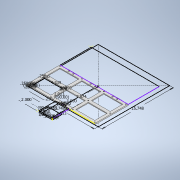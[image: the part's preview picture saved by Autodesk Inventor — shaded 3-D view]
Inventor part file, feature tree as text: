
AUTODESK INVENTOR PART (.ipt)
format: ipt  version: 2020 (Build 240168000, 168)  size: 369,664 bytes
history: native  units: in
note: dims shown in document units (in); Inventor stores cm internally (conversion verified against a paired STEP export)
features: extrude x8, sketch x7, hole x4, pattern_linear x1
ambient origin geometry x8: Origin, YZ Plane, XZ Plane, XY Plane, X Axis, Y Axis, Z Axis, Center Point
bodies: Solid1 (feature_tree)
feature tree (20):
  sketch  "Sketch1"  dims[d0=3.0in d1=2.0in]
  extrude  "Extrusion1"  Depth=2.0in
  hole  "Hole1"  [1 undecoded]
  sketch  "Sketch2"  dims[d2=0.25in d3=1.0in]
  extrude  "Extrusion2"  TaperAngle=0.0deg  [1 undecoded]
  hole  "Hole2"  [1 undecoded]
  extrude  "Extrusion3"  Depth=0.25in
  pattern_linear  "Rectangular Pattern1"  Spacing1=2.9528in  [1 undecoded]
  extrude  "Extrusion4"  Depth=0.25in
  sketch  "Sketch4"  dims[d6=0.5in d7=0.5in]
  extrude  "Extrusion5"  Depth=0.25in
  hole  "Hole3"  [1 undecoded]
  extrude  "Extrusion6"  Depth=0.25in
  extrude  "Extrusion7"  Depth=0.25in
  extrude  "Extrusion8"  Depth=0.25in TaperAngle=0.0deg
  hole  "Hole4"  [1 undecoded]
  sketch  "Sketch3"  dims[d4=1.0in d5=0.0in]
  sketch  "Sketch5"  dims[d8=0.25in d9=0.25in]
  sketch  "Sketch6"  dims[d10=2.9528in]
  sketch  "Sketch7"  dims[d11=90.0deg d12=2.9528in d13=1.0in d14=7.874in d15=90.0deg d16=15.748in d17=15.748in d18=0.25in d19=0.0in d20=0.26in d21=0.5in d22=0.375in d23=0.25in d24=0.5635in d25=1.0in d26=0.8108in d27=0.25in d28=90.0deg d29=0.25in d30=0.25in d31=0.25in d32=4.3386in d33=2.9134in d34=0.25in d35=0.25in d36=0.25in d37=0.25in d38=0.25in d39=0.315in d40=90.0deg d41=0.0787in d42=0.0787in d43=0.0787in d44=0.0787in d45=0.0in d46=0.0in d47=0.203in d48=0.625in d49=0.375in d50=0.25in d51=0.5635in d52=1.0in d53=0.8108in d54=0.0787in d55=0.0in d56=1.1811in d58=4.839in d59=1.5748in d61=3.423in d62=0.25in d63=0.25in d64=0.0in d65=0.0in d66=0.25in d67=0.5in d68=1.0in d69=1.0in d70=0.0in d71=0.266in d72=0.75in d73=0.438in d74=0.25in d75=0.5635in d76=1.0in d77=0.8108in d78=0.125in d79=2.0in d80=0.125in d81=0.125in d82=0.0in d83=1.25in d84=0.0in d85=0.125in d86=2.0in d87=0.125in d88=0.125in d89=2.0in d90=0.125in d91=0.125in d92=2.0in d93=0.125in d94=0.125in d95=0.0in d96=0.375in d97=0.5in d98=1.0in d99=0.375in d100=0.5in d101=1.0in d102=0.5in d103=1.0in d104=0.266in d105=0.75in d106=0.438in d107=0.25in d108=0.5635in d109=1.0in d110=0.8108in]
note: 6 required parameter values undecoded (feature->parameter linkage not recoverable at this tier; creation-order binding heuristic only, values carry confidence <= 0.55)
